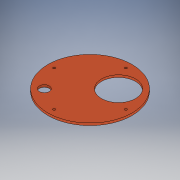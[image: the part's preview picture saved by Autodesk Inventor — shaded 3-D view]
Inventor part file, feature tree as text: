
AUTODESK INVENTOR PART (.ipt)
format: ipt  version: 2018 (Build 220112000, 112)  size: 139,776 bytes
history: native  units: in
note: dims shown in document units (in); Inventor stores cm internally (conversion verified against a paired STEP export)
features: sketch x4, extrude x2, hole x1
ambient origin geometry x8: Origin, YZ Plane, XZ Plane, XY Plane, X Axis, Y Axis, Z Axis, Center Point
bodies: Solid1 (feature_tree)
feature tree (7):
  extrude  "Extrusion1"  TaperAngle=135.0deg  [1 undecoded]
  extrude  "Extrusion2"  Depth=2.25in
  sketch  "Sketch9"  dims[d4=45.0deg d5=1.1in]
  hole  "Hole4"  [1 undecoded]
  sketch  "Sketch1"  dims[d0=3.6in d1=135.0deg]
  sketch  "Sketch2"  dims[d2=3.8in d3=2.25in]
  sketch  "Sketch10"  dims[d6=1.35in d7=315.0deg d8=9.375in d9=0.25in d10=0.0in d11=0.0in d12=0.0in d81=5.0in d82=5.0in d83=8.0in d84=1.5748in d86=360.0deg d88=0.266in d89=0.75in d90=0.507in d91=0.25in d92=0.5635in d93=1.0in d94=0.8108in]
note: 2 required parameter values undecoded (feature->parameter linkage not recoverable at this tier; creation-order binding heuristic only, values carry confidence <= 0.55)
